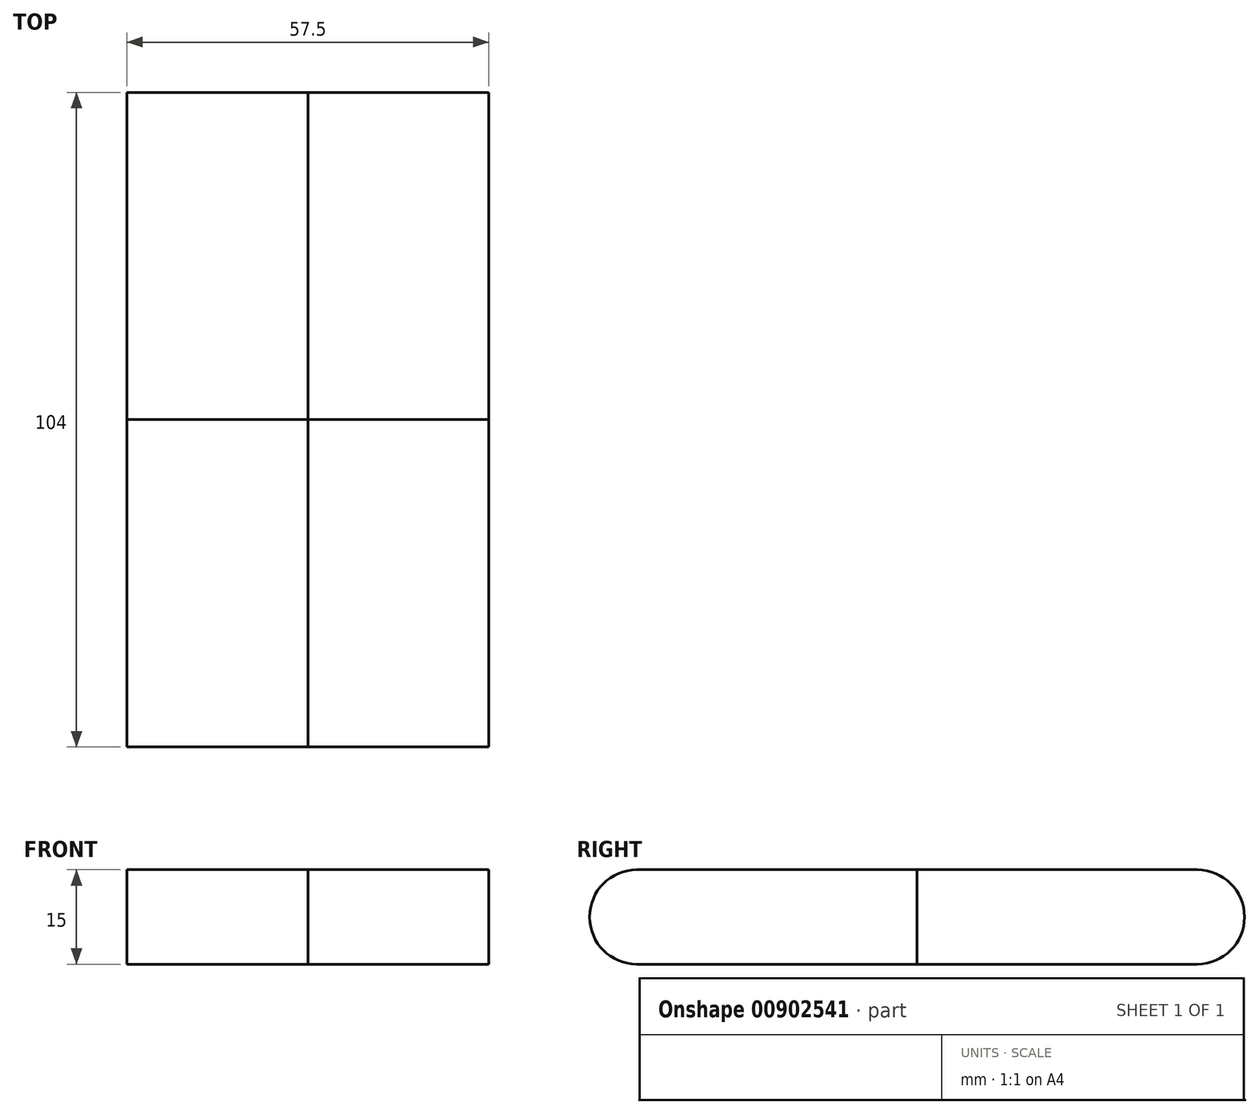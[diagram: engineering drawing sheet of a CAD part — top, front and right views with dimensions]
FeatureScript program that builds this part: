
annotation { "Feature Type Name" : "Feature", "Feature Type Description" : "" }
export const myFeature = defineFeature(function(context is Context, id is Id, definition is map)
    precondition{}
    {
        {
            var Q0;
            Q0=qCreatedBy(makeId("Top.planeOp"),FACE);
            var sketch = newSketch(context, id + "F0", { "sketchPlane" : qUnion([Q0])});
            skLineSegment(sketch, "E0.bottom", {"start": v(0, 0) * mm, "end": v(-28.75, 0) * mm});
            skLineSegment(sketch, "E0.top", {"start": v(0, 52) * mm, "end": v(-28.75, 52) * mm});
            skLineSegment(sketch, "E0.left", {"start": v(0, 0) * mm, "end": v(0, 52) * mm});
            skLineSegment(sketch, "E0.right", {"start": v(-28.75, 0) * mm, "end": v(-28.75, 52) * mm});
            skLineSegment(sketch, "E1.bottom", {"start": v(0, 0) * mm, "end": v(28.75, 0) * mm});
            skLineSegment(sketch, "E1.top", {"start": v(0, 52) * mm, "end": v(28.75, 52) * mm});
            skLineSegment(sketch, "E1.right", {"start": v(28.75, 0) * mm, "end": v(28.75, 52) * mm});
            skLineSegment(sketch, "E2.top", {"start": v(0, -52) * mm, "end": v(-28.75, -52) * mm});
            skLineSegment(sketch, "E2.left", {"start": v(0, 0) * mm, "end": v(0, -52) * mm});
            skLineSegment(sketch, "E2.right", {"start": v(-28.75, 0) * mm, "end": v(-28.75, -52) * mm});
            skLineSegment(sketch, "E3.top", {"start": v(0, -52) * mm, "end": v(28.75, -52) * mm});
            skLineSegment(sketch, "E3.right", {"start": v(28.75, 0) * mm, "end": v(28.75, -52) * mm});
            skSolve(sketch);
        }
        {
            var Q0;
            Q0=makeQuery(id+"F0.imprint","IMPRINT",FACE,{"disambiguationData":[TD([[makeQuery(id+"F0.imprint","IMPRINT",EDGE,{"derivedFrom":sQuery(id+"F0.wireOp",EDGE,"E0.top")}),1.0]])]});
            var Q1;
            Q1=makeQuery(id+"F0.imprint","IMPRINT",FACE,{"disambiguationData":[TD([[makeQuery(id+"F0.imprint","IMPRINT",EDGE,{"derivedFrom":sQuery(id+"F0.wireOp",EDGE,"E1.bottom")}),-1.0]])]});
            extrude(context, id + "F1", {"entities" : qUnion([Q0, Q1]), "depth" : 15 * mm, "offsetDistance" : 25 * mm, "symmetric" : true});
        }
        {
            var Q0;
            Q0=makeQuery(id+"F0.imprint","IMPRINT",FACE,{"disambiguationData":[TD([[makeQuery(id+"F0.imprint","IMPRINT",EDGE,{"derivedFrom":sQuery(id+"F0.wireOp",EDGE,"E1.top")}),-1.0]])]});
            var Q1;
            Q1=makeQuery(id+"F0.imprint","IMPRINT",FACE,{"disambiguationData":[TD([[makeQuery(id+"F0.imprint","IMPRINT",EDGE,{"derivedFrom":sQuery(id+"F0.wireOp",EDGE,"E0.bottom")}),1.0]])]});
            extrude(context, id + "F2", {"entities" : qUnion([Q0, Q1]), "depth" : 15 * mm, "offsetDistance" : 25 * mm, "symmetric" : true});
        }
        {
            var Q0;
            Q0=makeQuery(id+"F1.opExtrude","CAP_EDGE",EDGE,{"disambiguationData":[OSD([sQuery(id+"F0.wireOp",EDGE,"E0.top")])],"isStart":false});
            var Q1;
            Q1=makeQuery(id+"F2.opExtrude","CAP_EDGE",EDGE,{"disambiguationData":[OSD([sQuery(id+"F0.wireOp",EDGE,"E1.top")])],"isStart":false});
            var Q2;
            Q2=makeQuery(id+"F1.opExtrude","CAP_EDGE",EDGE,{"disambiguationData":[OSD([sQuery(id+"F0.wireOp",EDGE,"E0.top")])],"isStart":true});
            var Q3;
            Q3=makeQuery(id+"F2.opExtrude","CAP_EDGE",EDGE,{"disambiguationData":[OSD([sQuery(id+"F0.wireOp",EDGE,"E1.top")])],"isStart":true});
            var Q4;
            Q4=makeQuery(id+"F1.opExtrude","CAP_EDGE",EDGE,{"disambiguationData":[OSD([sQuery(id+"F0.wireOp",EDGE,"E3.top")])],"isStart":false});
            var Q5;
            Q5=makeQuery(id+"F2.opExtrude","CAP_EDGE",EDGE,{"disambiguationData":[OSD([sQuery(id+"F0.wireOp",EDGE,"E2.top")])],"isStart":false});
            var Q6;
            Q6=makeQuery(id+"F1.opExtrude","CAP_EDGE",EDGE,{"disambiguationData":[OSD([sQuery(id+"F0.wireOp",EDGE,"E3.top")])],"isStart":true});
            var Q7;
            Q7=makeQuery(id+"F2.opExtrude","CAP_EDGE",EDGE,{"disambiguationData":[OSD([sQuery(id+"F0.wireOp",EDGE,"E2.top")])],"isStart":true});
            fillet(context, id + "F3", {"entities" : qUnion([Q0, Q1, Q2, Q3, Q4, Q5, Q6, Q7]), "radius" : 7.5 * mm, "tangentPropagation" : true, "allowEdgeOverflow" : false});
        }
    });
